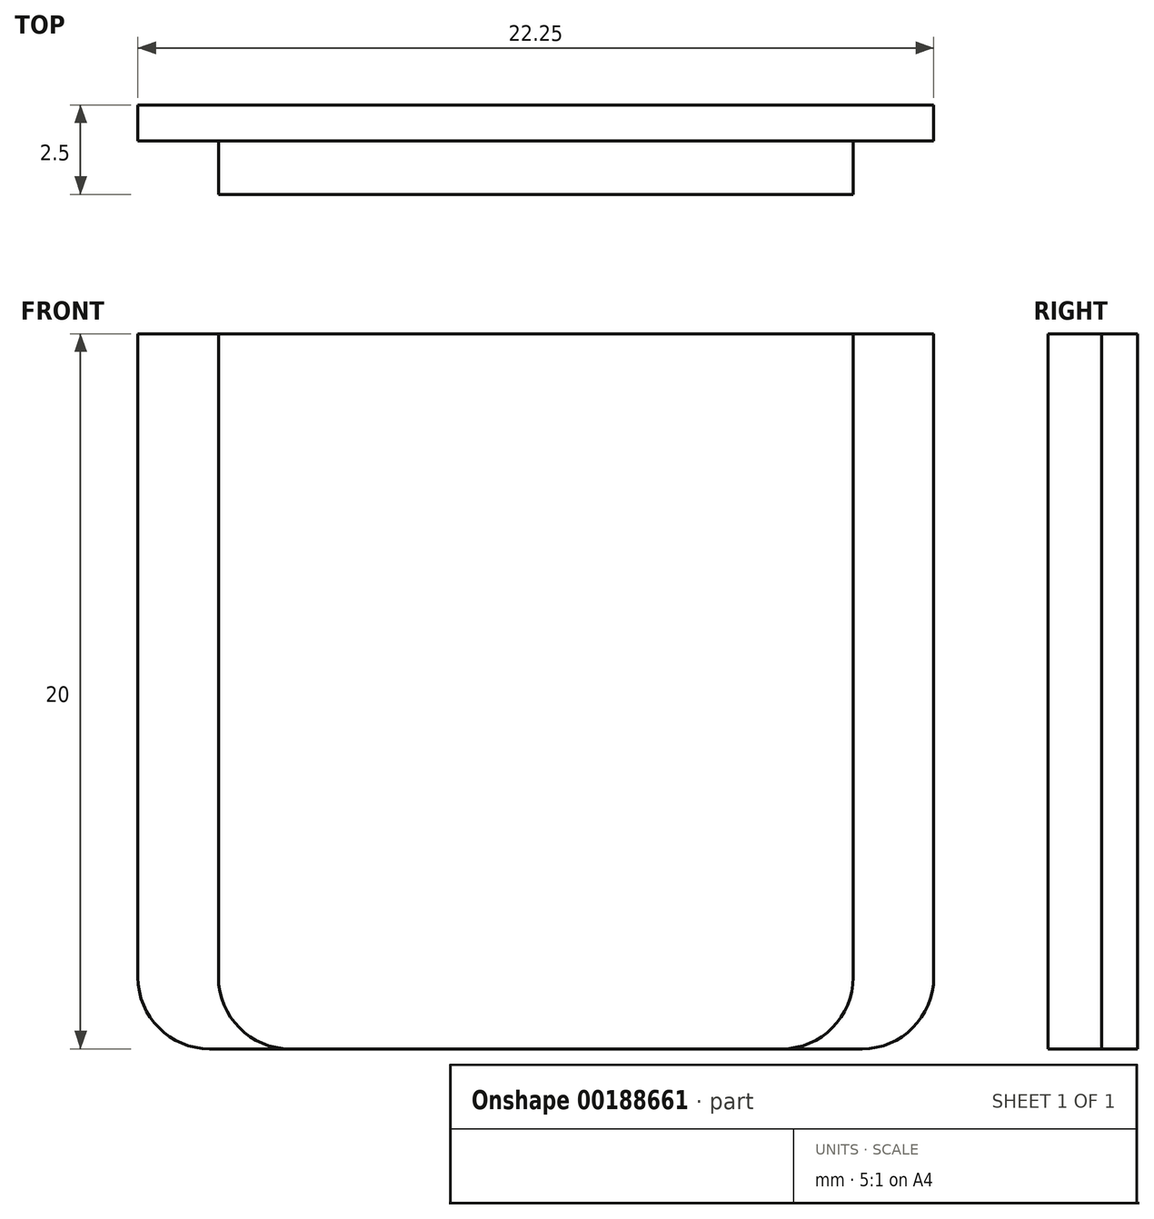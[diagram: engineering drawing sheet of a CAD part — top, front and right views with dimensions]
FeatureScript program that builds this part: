
annotation { "Feature Type Name" : "Feature", "Feature Type Description" : "" }
export const myFeature = defineFeature(function(context is Context, id is Id, definition is map)
    precondition{}
    {
        {
            var Q0;
            Q0=qCreatedBy(makeId("Front.planeOp"),FACE);
            var sketch = newSketch(context, id + "F0", { "sketchPlane" : qUnion([Q0])});
            skLineSegment(sketch, "E0.bottom", {"start": v(2, 0) * mm, "end": v(20.25, 0) * mm});
            skLineSegment(sketch, "E0.top", {"start": v(0, 20) * mm, "end": v(22.25, 20) * mm});
            skLineSegment(sketch, "E0.left", {"start": v(0, 2) * mm, "end": v(0, 20) * mm});
            skLineSegment(sketch, "E0.right", {"start": v(22.25, 2) * mm, "end": v(22.25, 20) * mm});
            skPoint(sketch, "E1.visualSharp", {"position": v(0, 0) * mm});
            skArc(sketch, "E1.filletArc", {"start": v(0, 2) * mm, "mid": v(0.59, 0.59) * mm, "end": v(2, 0) * mm});
            skPoint(sketch, "E2.visualSharp", {"position": v(22.25, 0) * mm});
            skArc(sketch, "E2.filletArc", {"start": v(20.25, 0) * mm, "mid": v(21.66, 0.59) * mm, "end": v(22.25, 2) * mm});
            skSolve(sketch);
        }
        {
            var Q0;
            Q0=qSketchRegion(id+"F0",true);
            extrude(context, id + "F1", {"entities" : qUnion([Q0]), "depth" : 1 * mm});
        }
        {
            var Q0;
            Q0=makeQuery(id+"F1.opExtrude","CAP_FACE",FACE,{"disambiguationData":[OSD([sQuery(id+"F0.wireOp",EDGE,"E0.bottom"),sQuery(id+"F0.wireOp",EDGE,"E0.top"),sQuery(id+"F0.wireOp",EDGE,"E0.left"),sQuery(id+"F0.wireOp",EDGE,"E0.right")])],"isStart":false});
            var sketch = newSketch(context, id + "F2", { "sketchPlane" : qUnion([Q0])});
            skLineSegment(sketch, "E3.bottom", {"start": v(2.25, 20) * mm, "end": v(20, 20) * mm});
            skLineSegment(sketch, "E3.top", {"start": v(4.25, 0) * mm, "end": v(18, 0) * mm});
            skLineSegment(sketch, "E3.left", {"start": v(2.25, 20) * mm, "end": v(2.25, 2) * mm});
            skLineSegment(sketch, "E3.right", {"start": v(20, 20) * mm, "end": v(20, 2) * mm});
            skPoint(sketch, "E4", {"position": v(11.12, 20) * mm});
            skPoint(sketch, "E5.visualSharp", {"position": v(2.25, 0) * mm});
            skArc(sketch, "E5.filletArc", {"start": v(2.25, 2) * mm, "mid": v(2.84, 0.59) * mm, "end": v(4.25, 0) * mm});
            skPoint(sketch, "E6.visualSharp", {"position": v(20, 0) * mm});
            skArc(sketch, "E6.filletArc", {"start": v(18, 0) * mm, "mid": v(19.41, 0.59) * mm, "end": v(20, 2) * mm});
            skSolve(sketch);
        }
        {
            var Q0;
            Q0=qSketchRegion(id+"F2",true);
            extrude(context, id + "F3", {"entities" : qUnion([Q0]), "depth" : 1.5 * mm});
        }
    });
